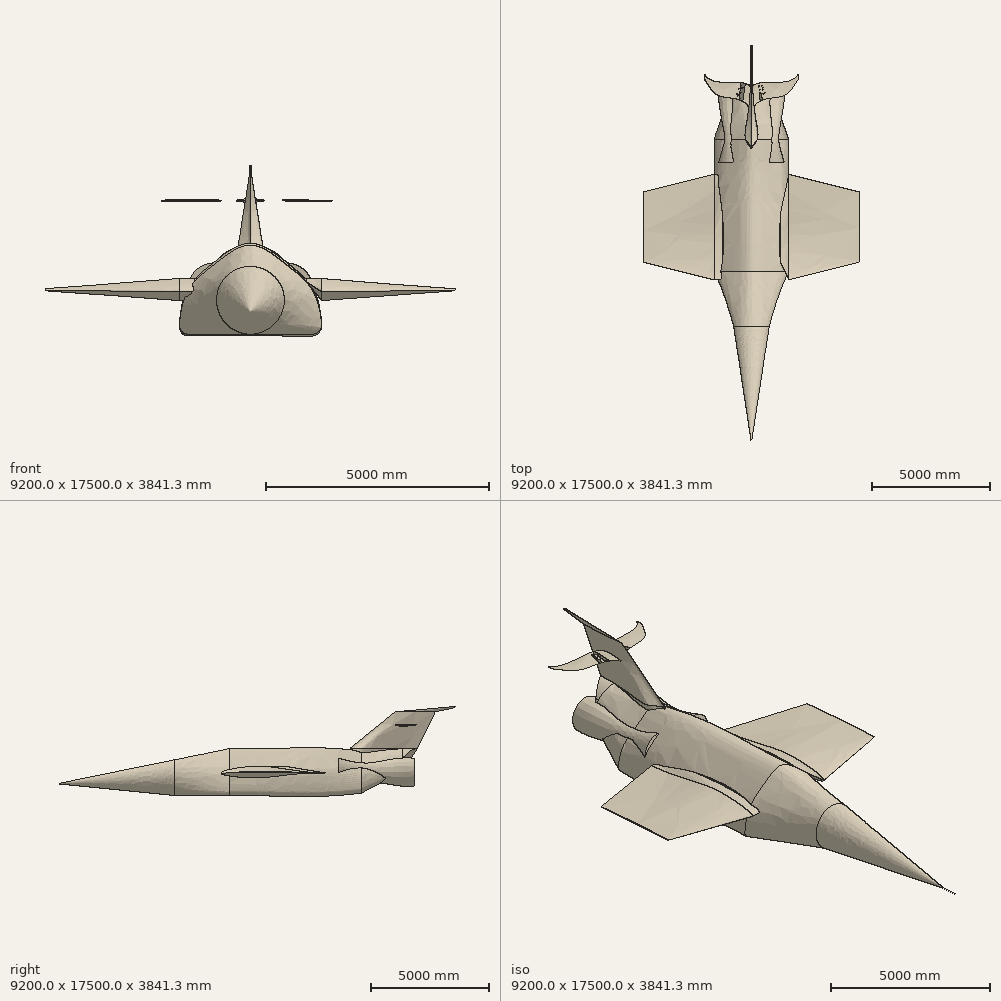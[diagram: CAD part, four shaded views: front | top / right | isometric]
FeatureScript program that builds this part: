
annotation { "Feature Type Name" : "Feature", "Feature Type Description" : "" }
export const myFeature = defineFeature(function(context is Context, id is Id, definition is map)
    precondition{}
    {
        {
            var Q0;
            Q0=qCreatedBy(makeId("Right.planeOp"),FACE);
            var sketch = newSketch(context, id + "F0", { "sketchPlane" : qUnion([Q0])});
            skLineSegment(sketch, "E0", {"start": v(0, 0) * mm, "end": v(-1750, 0) * mm});
            skLineSegment(sketch, "E1", {"start": v(-1750, 0) * mm, "end": v(-3500, 0) * mm});
            skLineSegment(sketch, "E2", {"start": v(-3500, 0) * mm, "end": v(-3500, -1000) * mm});
            skLineSegment(sketch, "E3", {"start": v(-3500, -1000) * mm, "end": v(-8500, -1000) * mm});
            skLineSegment(sketch, "E4", {"start": v(-8500, -1000) * mm, "end": v(-8500, -499.31) * mm});
            skLineSegment(sketch, "E5", {"start": v(-1151.4, 0) * mm, "end": v(-1151.4, 1000) * mm});
            skLineSegment(sketch, "E6", {"start": v(-1151.4, 1000) * mm, "end": v(-8500, -499.31) * mm});
            skLineSegment(sketch, "E7", {"start": v(-8500, -499.31) * mm, "end": v(-3500, -1000) * mm});
            skLineSegment(sketch, "E8", {"start": v(-3500, 0) * mm, "end": v(-3500, 520.82) * mm});
            skLineSegment(sketch, "E9", {"start": v(-8500, -499.31) * mm, "end": v(-8450, -499.31) * mm});
            skLineSegment(sketch, "E10", {"start": v(-8450, -499.31) * mm, "end": v(-8450, -489.1) * mm});
            skLineSegment(sketch, "E11", {"start": v(-8450, -499.31) * mm, "end": v(-8450, -504.32) * mm});
            skSolve(sketch);
        }
        {
            var Q0;
            Q0=sQuery(id+"F0.wireOp",EDGE,"E5");
            cPlane(context, id + "F1", {"entities" : qUnion([Q0]), "cplaneType" : CPlaneType.LINE_ANGLE, "offset" : 25 * mm, "angle" : 90 * degree, "oppositeDirection" : true, "width" : 150 * mm, "height" : 150 * mm});
        }
        {
            var Q0;
            Q0=qCreatedBy(id+"F1.planeOp",FACE);
            var sketch = newSketch(context, id + "F2", { "sketchPlane" : qUnion([Q0])});
            skLineSegment(sketch, "E12.top", {"start": v(-1394.2, -1000) * mm, "end": v(1394.2, -1000) * mm});
            skPoint(sketch, "E12.middle", {"position": v(0, 0) * mm});
            skFitSpline(sketch, "E13", {"points": [v(-1600, -1000) * mm, v(-848, 530) * mm, v(0, 1000) * mm, v(848, 530) * mm, v(1600, -1000) * mm], "startDerivative": vector(0, 10524.75) * mm, "endDerivative": vector(0, -10524.75) * mm});
            skArc(sketch, "E14", {"start": v(-735.27, 618.52) * mm, "mid": v(-1273.27, 435.52) * mm, "end": v(-1440.68, -107.53) * mm});
            skArc(sketch, "E15", {"start": v(1440.68, -107.53) * mm, "mid": v(1273.27, 435.52) * mm, "end": v(735.27, 618.52) * mm});
            skFitSpline(sketch, "E16.trimOffspring", {"points": [v(-1600, -1000) * mm, v(-848, 530) * mm, v(0, 1000) * mm, v(848, 530) * mm, v(1600, -1000) * mm], "startDerivative": vector(0, 10524.75) * mm, "endDerivative": vector(0, -10524.75) * mm});
            skFitSpline(sketch, "E17.trimOffspring", {"points": [v(-1600, -1000) * mm, v(-848, 530) * mm, v(0, 1000) * mm, v(848, 530) * mm, v(1600, -1000) * mm], "startDerivative": vector(0, 10524.75) * mm, "endDerivative": vector(0, -10524.75) * mm});
            skArc(sketch, "E18.filletArc", {"start": v(-1593.82, -787.83) * mm, "mid": v(-1539.85, -937.05) * mm, "end": v(-1394.2, -1000) * mm});
            skArc(sketch, "E19.filletArc", {"start": v(1394.2, -1000) * mm, "mid": v(1539.85, -937.05) * mm, "end": v(1593.82, -787.83) * mm});
            skSolve(sketch);
        }
        {
            var Q0;
            Q0=qCreatedBy(makeId("Front.planeOp"),FACE);
            var sketch = newSketch(context, id + "F3", { "sketchPlane" : qUnion([Q0])});
            skLineSegment(sketch, "E20.top", {"start": v(-1394.2, -1000) * mm, "end": v(1394.2, -1000) * mm});
            skPoint(sketch, "E20.middle", {"position": v(0, 0) * mm});
            skFitSpline(sketch, "E21", {"points": [v(-1600, -1000) * mm, v(-848, 530) * mm, v(0, 1000) * mm, v(848, 530) * mm, v(1600, -1000) * mm], "startDerivative": vector(0, 10524.75) * mm, "endDerivative": vector(0, -10524.75) * mm});
            skArc(sketch, "E22", {"start": v(-735.27, 618.52) * mm, "mid": v(-1273.27, 435.52) * mm, "end": v(-1440.68, -107.53) * mm});
            skArc(sketch, "E23", {"start": v(1440.68, -107.53) * mm, "mid": v(1273.27, 435.52) * mm, "end": v(735.27, 618.52) * mm});
            skFitSpline(sketch, "E24.trimOffspring", {"points": [v(-1600, -1000) * mm, v(-848, 530) * mm, v(0, 1000) * mm, v(848, 530) * mm, v(1600, -1000) * mm], "startDerivative": vector(0, 10524.75) * mm, "endDerivative": vector(0, -10524.75) * mm});
            skFitSpline(sketch, "E25.trimOffspring", {"points": [v(-1600, -1000) * mm, v(-848, 530) * mm, v(0, 1000) * mm, v(848, 530) * mm, v(1600, -1000) * mm], "startDerivative": vector(0, 10524.75) * mm, "endDerivative": vector(0, -10524.75) * mm});
            skArc(sketch, "E26.filletArc", {"start": v(-1593.82, -787.83) * mm, "mid": v(-1539.85, -937.05) * mm, "end": v(-1394.2, -1000) * mm});
            skArc(sketch, "E27.filletArc", {"start": v(1394.2, -1000) * mm, "mid": v(1539.85, -937.05) * mm, "end": v(1593.82, -787.83) * mm});
            skSolve(sketch);
        }
        {
            var Q0;
            Q0=qCreatedBy(makeId("Front.planeOp"),FACE);
            cPlane(context, id + "F4", {"entities" : qUnion([Q0]), "cplaneType" : CPlaneType.OFFSET, "offset" : 3500 * mm, "oppositeDirection" : true, "width" : 150 * mm, "height" : 150 * mm});
        }
        {
            var Q0;
            Q0=qCreatedBy(id+"F4.planeOp",FACE);
            var sketch = newSketch(context, id + "F5", { "sketchPlane" : qUnion([Q0])});
            skLineSegment(sketch, "E28.top", {"start": v(-1394.2, -1000) * mm, "end": v(1394.2, -1000) * mm});
            skPoint(sketch, "E28.middle", {"position": v(0, 0) * mm});
            skFitSpline(sketch, "E29", {"points": [v(-1600, -1000) * mm, v(-848, 530) * mm, v(0, 1000) * mm, v(848, 530) * mm, v(1600, -1000) * mm], "startDerivative": vector(0, 10524.75) * mm, "endDerivative": vector(0, -10524.75) * mm});
            skArc(sketch, "E30", {"start": v(-735.27, 618.52) * mm, "mid": v(-1273.27, 435.52) * mm, "end": v(-1440.68, -107.53) * mm});
            skArc(sketch, "E31", {"start": v(1440.68, -107.53) * mm, "mid": v(1273.27, 435.52) * mm, "end": v(735.27, 618.52) * mm});
            skFitSpline(sketch, "E32.trimOffspring", {"points": [v(-1600, -1000) * mm, v(-848, 530) * mm, v(0, 1000) * mm, v(848, 530) * mm, v(1600, -1000) * mm], "startDerivative": vector(0, 10524.75) * mm, "endDerivative": vector(0, -10524.75) * mm});
            skFitSpline(sketch, "E33.trimOffspring", {"points": [v(-1600, -1000) * mm, v(-848, 530) * mm, v(0, 1000) * mm, v(848, 530) * mm, v(1600, -1000) * mm], "startDerivative": vector(0, 10524.75) * mm, "endDerivative": vector(0, -10524.75) * mm});
            skArc(sketch, "E34.filletArc", {"start": v(-1593.82, -787.83) * mm, "mid": v(-1539.85, -937.05) * mm, "end": v(-1394.2, -1000) * mm});
            skArc(sketch, "E35.filletArc", {"start": v(1394.2, -1000) * mm, "mid": v(1539.85, -937.05) * mm, "end": v(1593.82, -787.83) * mm});
            skSolve(sketch);
        }
        {
            var Q0;
            Q0=qCreatedBy(makeId("Front.planeOp"),FACE);
            cPlane(context, id + "F6", {"entities" : qUnion([Q0]), "cplaneType" : CPlaneType.OFFSET, "offset" : 4500 * mm, "oppositeDirection" : true, "width" : 150 * mm, "height" : 150 * mm});
        }
        {
            var Q0;
            Q0=qCreatedBy(id+"F6.planeOp",FACE);
            var sketch = newSketch(context, id + "F7", { "sketchPlane" : qUnion([Q0])});
            skLineSegment(sketch, "E36.top", {"start": v(-1413.07, -900) * mm, "end": v(1413.07, -900) * mm});
            skPoint(sketch, "E36.middle", {"position": v(0, 0) * mm});
            skFitSpline(sketch, "E37", {"points": [v(-1600, -900) * mm, v(-784.42, 441.24) * mm, v(0, 900) * mm, v(784.42, 441.24) * mm, v(1600, -900) * mm], "startDerivative": vector(0, 9508.62) * mm, "endDerivative": vector(0, -9508.62) * mm});
            skArc(sketch, "E38", {"start": v(-719.25, 488.69) * mm, "mid": v(-1131.76, 394.84) * mm, "end": v(-1324.66, 18.33) * mm});
            skArc(sketch, "E39", {"start": v(1324.66, 18.33) * mm, "mid": v(1131.76, 394.84) * mm, "end": v(719.25, 488.69) * mm});
            skFitSpline(sketch, "E40.trimOffspring", {"points": [v(-1600, -900) * mm, v(-784.42, 441.24) * mm, v(0, 900) * mm, v(784.42, 441.24) * mm, v(1600, -900) * mm], "startDerivative": vector(0, 9508.62) * mm, "endDerivative": vector(0, -9508.62) * mm});
            skFitSpline(sketch, "E41.trimOffspring", {"points": [v(-1600, -900) * mm, v(-784.42, 441.24) * mm, v(0, 900) * mm, v(784.42, 441.24) * mm, v(1600, -900) * mm], "startDerivative": vector(0, 9508.62) * mm, "endDerivative": vector(0, -9508.62) * mm});
            skArc(sketch, "E42.filletArc", {"start": v(-1592.48, -705.43) * mm, "mid": v(-1545.4, -842.02) * mm, "end": v(-1413.07, -900) * mm});
            skArc(sketch, "E43.filletArc", {"start": v(1413.07, -900) * mm, "mid": v(1545.4, -842.02) * mm, "end": v(1592.48, -705.43) * mm});
            skLineSegment(sketch, "E44", {"start": v(-719.25, 488.69) * mm, "end": v(-1324.66, 18.33) * mm, "construction": true});
            skLineSegment(sketch, "E45", {"start": v(719.25, 488.69) * mm, "end": v(1324.66, 18.33) * mm, "construction": true});
            skSolve(sketch);
        }
        {
            var Q0;
            Q0=qCreatedBy(makeId("Front.planeOp"),FACE);
            cPlane(context, id + "F8", {"entities" : qUnion([Q0]), "cplaneType" : CPlaneType.OFFSET, "offset" : 6232.05 * mm, "oppositeDirection" : true, "width" : 150 * mm, "height" : 150 * mm});
        }
        {
            var Q0;
            Q0=qCreatedBy(id+"F8.planeOp",FACE);
            var sketch = newSketch(context, id + "F9", { "sketchPlane" : qUnion([Q0])});
            skArc(sketch, "E46", {"start": v(998.61, 52.63) * mm, "mid": v(0, 1000) * mm, "end": v(-998.61, 52.63) * mm});
            skLineSegment(sketch, "E47", {"start": v(0, 0) * mm, "end": v(-948.68, 0) * mm});
            skLineSegment(sketch, "E48", {"start": v(0, 0) * mm, "end": v(948.68, 0) * mm});
            skLineSegment(sketch, "E49", {"start": v(0, 1000) * mm, "end": v(0, 675) * mm, "construction": true});
            skLineSegment(sketch, "E50", {"start": v(0, 675) * mm, "end": v(-737.82, 675) * mm, "construction": true});
            skLineSegment(sketch, "E51", {"start": v(0, 675) * mm, "end": v(737.82, 675) * mm, "construction": true});
            skPoint(sketch, "E52.visualSharp", {"position": v(-1000, 0) * mm});
            skArc(sketch, "E52.filletArc", {"start": v(-998.61, 52.63) * mm, "mid": v(-984.96, 15.59) * mm, "end": v(-948.68, 0) * mm});
            skPoint(sketch, "E53.visualSharp", {"position": v(1000, 0) * mm});
            skArc(sketch, "E53.filletArc", {"start": v(948.68, 0) * mm, "mid": v(984.96, 15.59) * mm, "end": v(998.61, 52.63) * mm});
            skSolve(sketch);
        }
        {
            var Q0;
            Q0=makeQuery(id+"F2.imprint","IMPRINT",FACE,{"disambiguationData":[TD([[makeQuery(id+"F2.imprint","IMPRINT",EDGE,{"derivedFrom":sQuery(id+"F2.wireOp",EDGE,"E12.top")}),1.0]])]});
            var Q1;
            Q1=makeQuery(id+"F3.imprint","IMPRINT",FACE,{"disambiguationData":[TD([[makeQuery(id+"F3.imprint","IMPRINT",EDGE,{"derivedFrom":sQuery(id+"F3.wireOp",EDGE,"E20.top")}),1.0]])]});
            var Q2;
            Q2=makeQuery(id+"F5.imprint","IMPRINT",FACE,{"disambiguationData":[TD([[makeQuery(id+"F5.imprint","IMPRINT",EDGE,{"derivedFrom":sQuery(id+"F5.wireOp",EDGE,"E28.top")}),1.0]])]});
            var Q3;
            Q3=makeQuery(id+"F7.imprint","IMPRINT",FACE,{"disambiguationData":[TD([[makeQuery(id+"F7.imprint","IMPRINT",EDGE,{"derivedFrom":sQuery(id+"F7.wireOp",EDGE,"E36.top")}),1.0]])]});
            loft(context, id + "F10", {"sheetProfilesArray" : [{ "sheetProfileEntities" : qUnion([Q0]) }, { "sheetProfileEntities" : qUnion([Q1]) }, { "sheetProfileEntities" : qUnion([Q2]) }, { "sheetProfileEntities" : qUnion([Q3]) }]});
        }
        {
            var Q0;
            Q0=sQuery(id+"F7.wireOp",EDGE,"E44");
            var Q1;
            Q1=sQuery(id+"F9.wireOp",VERTEX,"E50.end");
            cPlane(context, id + "F11", {"entities" : qUnion([Q0, Q1]), "cplaneType" : CPlaneType.LINE_ANGLE, "offset" : 25 * mm, "angle" : 180 * degree, "width" : 150 * mm, "height" : 150 * mm});
        }
        {
            var Q0;
            Q0=qCreatedBy(id+"F11.planeOp",FACE);
            var sketch = newSketch(context, id + "F12", { "sketchPlane" : qUnion([Q0])});
            skLineSegment(sketch, "E54", {"start": v(-589.34, 4526.34) * mm, "end": v(-612.8, 6268.32) * mm});
            skLineSegment(sketch, "E55", {"start": v(-1354.08, 4472.19) * mm, "end": v(-612.8, 6268.32) * mm});
            skSolve(sketch);
        }
        {
            var Q0;
            Q0=sQuery(id+"F7.wireOp",EDGE,"E45");
            var Q1;
            Q1=sQuery(id+"F9.wireOp",VERTEX,"E51.end");
            cPlane(context, id + "F13", {"entities" : qUnion([Q0, Q1]), "cplaneType" : CPlaneType.LINE_ANGLE, "offset" : 25 * mm, "angle" : 0 * degree, "width" : 150 * mm, "height" : 150 * mm});
        }
        {
            var Q0;
            Q0=qCreatedBy(id+"F13.planeOp",FACE);
            var sketch = newSketch(context, id + "F14", { "sketchPlane" : qUnion([Q0])});
            skLineSegment(sketch, "E56", {"start": v(589.34, 4526.34) * mm, "end": v(612.8, 6268.32) * mm});
            skLineSegment(sketch, "E57", {"start": v(1354.08, 4472.19) * mm, "end": v(612.8, 6268.32) * mm});
            skSolve(sketch);
        }
        {
            var Q1;
            Q1=makeQuery(id+"F10.opLoft","CAP_FACE",FACE,{"disambiguationData":[OSD([makeQuery(id+"F7.imprint","IMPRINT",FACE,{"disambiguationData":[TD([[makeQuery(id+"F7.imprint","IMPRINT",EDGE,{"derivedFrom":sQuery(id+"F7.wireOp",EDGE,"E36.top")}),1.0]])]})])],"isStart":true});
            var Q2;
            Q2=makeQuery(id+"F9.imprint","IMPRINT",FACE,{"disambiguationData":[TD([[makeQuery(id+"F9.imprint","IMPRINT",EDGE,{"derivedFrom":sQuery(id+"F9.wireOp",EDGE,"E46")}),1.0]])]});
            var Q3;
            Q3=sQuery(id+"F12.wireOp",EDGE,"E54");
            var Q4;
            Q4=sQuery(id+"F14.wireOp",EDGE,"E56");
            loft(context, id + "F15", {"operationType" : NewBodyOperationType.ADD, "addGuides" : true, "sheetProfilesArray" : [{ "sheetProfileEntities" : qUnion([Q1]) }, { "sheetProfileEntities" : qUnion([Q2]) }], "guidesArray" : [{ "guideEntities" : qUnion([Q3]), "guideDerivativeType" : LoftGuideDerivativeType.DEFAULT, "guideDerivativeMagnitude" : 1 }, { "guideEntities" : qUnion([Q4]), "guideDerivativeType" : LoftGuideDerivativeType.DEFAULT, "guideDerivativeMagnitude" : 1 }]});
        }
        {
            var Q0;
            Q0=makeQuery(id+"F15.opLoft","CAP_FACE",FACE,{"disambiguationData":[OSD([makeQuery(id+"F9.imprint","IMPRINT",FACE,{"disambiguationData":[TD([[makeQuery(id+"F9.imprint","IMPRINT",EDGE,{"derivedFrom":sQuery(id+"F9.wireOp",EDGE,"E46")}),1.0]])]})])],"isStart":true});
            extrude(context, id + "F16", {"entities" : qUnion([Q0]), "operationType" : NewBodyOperationType.ADD, "depth" : 649.4 * mm, "offsetDistance" : 25 * mm});
        }
        {
            var Q0;
            Q0=qCreatedBy(makeId("Right.planeOp"),FACE);
            var sketch = newSketch(context, id + "F17", { "sketchPlane" : qUnion([Q0])});
            skLineSegment(sketch, "E58", {"start": v(0, 0) * mm, "end": v(4500, 0) * mm});
            skLineSegment(sketch, "E59", {"start": v(4500, 0) * mm, "end": v(6232.05, 0) * mm});
            skLineSegment(sketch, "E60", {"start": v(4500, 0) * mm, "end": v(4500, 1000) * mm});
            skLineSegment(sketch, "E61", {"start": v(4500, 1000) * mm, "end": v(6881.46, 1000) * mm});
            skLineSegment(sketch, "E62", {"start": v(6881.46, 1000) * mm, "end": v(6881.46, -1000) * mm});
            skLineSegment(sketch, "E63", {"start": v(6881.46, 1000) * mm, "end": v(6232.05, 0) * mm});
            skLineSegment(sketch, "E64", {"start": v(6232.05, 0) * mm, "end": v(5582.64, -1000) * mm});
            skLineSegment(sketch, "E65", {"start": v(5582.64, -1000) * mm, "end": v(6881.46, -1000) * mm});
            skSolve(sketch);
        }
        {
            var Q0;
            Q0=makeQuery(id+"F17.imprint","IMPRINT",FACE,{"disambiguationData":[TD([[makeQuery(id+"F17.imprint","IMPRINT",EDGE,{"derivedFrom":sQuery(id+"F17.wireOp",EDGE,"E62")}),-1.0]])]});
            var Q1;
            Q1=sQuery(id+"F17.wireOp",EDGE,"E61");
            revolve(context, id + "F18", {"operationType" : NewBodyOperationType.REMOVE, "entities" : qUnion([Q0]), "axis" : qUnion([Q1]), "revolveType" : RevolveType.SYMMETRIC, "oppositeDirection" : true, "angle" : 182 * degree});
        }
        {
            var Q0;
            Q0=qCreatedBy(id+"F1.planeOp",FACE);
            var sketch = newSketch(context, id + "F19", { "sketchPlane" : qUnion([Q0])});
            skLineSegment(sketch, "E66.top", {"start": v(-1394.2, -1000) * mm, "end": v(1394.2, -1000) * mm});
            skPoint(sketch, "E66.middle", {"position": v(0, 0) * mm});
            skFitSpline(sketch, "E67", {"points": [v(-1600, -1000) * mm, v(-848, 530) * mm, v(0, 1000) * mm, v(848, 530) * mm, v(1600, -1000) * mm], "startDerivative": vector(0, 10524.75) * mm, "endDerivative": vector(0, -10524.75) * mm});
            skArc(sketch, "E68.filletArc", {"start": v(-1593.82, -787.83) * mm, "mid": v(-1539.85, -937.05) * mm, "end": v(-1394.2, -1000) * mm});
            skArc(sketch, "E69.filletArc", {"start": v(1394.2, -1000) * mm, "mid": v(1539.85, -937.05) * mm, "end": v(1593.82, -787.83) * mm});
            skLineSegment(sketch, "E70", {"start": v(-1593.82, -787.83) * mm, "end": v(-1394.2, -1000) * mm, "construction": true});
            skLineSegment(sketch, "E71", {"start": v(1593.82, -787.83) * mm, "end": v(1394.2, -1000) * mm, "construction": true});
            skSolve(sketch);
        }
        {
            var Q0;
            Q0=qCreatedBy(makeId("Front.planeOp"),FACE);
            cPlane(context, id + "F20", {"entities" : qUnion([Q0]), "cplaneType" : CPlaneType.OFFSET, "offset" : 3500 * mm, "width" : 150 * mm, "height" : 150 * mm});
        }
        {
            var Q0;
            Q0=qCreatedBy(id+"F20.planeOp",FACE);
            var sketch = newSketch(context, id + "F21", { "sketchPlane" : qUnion([Q0])});
            skCircle(sketch, "E72", {"center": v(0, -239.59) * mm, "radius": 760.41 * mm});
            skLineSegment(sketch, "E73", {"start": v(0, -1000) * mm, "end": v(0, -800) * mm, "construction": true});
            skLineSegment(sketch, "E74", {"start": v(0, -800) * mm, "end": v(-513.97, -800) * mm, "construction": true});
            skLineSegment(sketch, "E75", {"start": v(0, -800) * mm, "end": v(513.97, -800) * mm, "construction": true});
            skSolve(sketch);
        }
        {
            var Q0;
            Q0=qCreatedBy(makeId("Front.planeOp"),FACE);
            cPlane(context, id + "F22", {"entities" : qUnion([Q0]), "cplaneType" : CPlaneType.OFFSET, "offset" : 8450 * mm, "width" : 150 * mm, "height" : 150 * mm});
        }
        {
            var Q0;
            Q0=qCreatedBy(id+"F22.planeOp",FACE);
            var sketch = newSketch(context, id + "F23", { "sketchPlane" : qUnion([Q0])});
            skCircle(sketch, "E76", {"center": v(0, -496.71) * mm, "radius": 7.6 * mm});
            skSolve(sketch);
        }
        {
            var Q0;
            Q0=sQuery(id+"F19.wireOp",EDGE,"E70");
            var Q1;
            Q1=sQuery(id+"F21.wireOp",VERTEX,"E74.end");
            cPlane(context, id + "F24", {"entities" : qUnion([Q0, Q1]), "cplaneType" : CPlaneType.LINE_ANGLE, "offset" : 25 * mm, "angle" : 0 * degree, "width" : 150 * mm, "height" : 150 * mm});
        }
        {
            var Q0;
            Q0=qCreatedBy(id+"F24.planeOp",FACE);
            var sketch = newSketch(context, id + "F25", { "sketchPlane" : qUnion([Q0])});
            skLineSegment(sketch, "E77", {"start": v(3032.27, -230.44) * mm, "end": v(558.11, 518.4) * mm});
            skLineSegment(sketch, "E78", {"start": v(3032.27, -230.44) * mm, "end": v(558.11, 227.09) * mm});
            skSolve(sketch);
        }
        {
            var Q0;
            Q0=sQuery(id+"F19.wireOp",EDGE,"E71");
            var Q1;
            Q1=sQuery(id+"F21.wireOp",VERTEX,"E75.end");
            cPlane(context, id + "F26", {"entities" : qUnion([Q0, Q1]), "cplaneType" : CPlaneType.LINE_ANGLE, "offset" : 25 * mm, "angle" : 180 * degree, "width" : 150 * mm, "height" : 150 * mm});
        }
        {
            var Q0;
            Q0=qCreatedBy(id+"F26.planeOp",FACE);
            var sketch = newSketch(context, id + "F27", { "sketchPlane" : qUnion([Q0])});
            skLineSegment(sketch, "E79", {"start": v(-3032.27, -230.44) * mm, "end": v(-558.11, 518.4) * mm});
            skLineSegment(sketch, "E80", {"start": v(-3032.27, -230.44) * mm, "end": v(-558.11, 227.09) * mm});
            skSolve(sketch);
        }
        {
            var Q1;
            Q1=makeQuery(id+"F19.imprint","IMPRINT",FACE,{"disambiguationData":[TD([[makeQuery(id+"F19.imprint","IMPRINT",EDGE,{"derivedFrom":sQuery(id+"F19.wireOp",EDGE,"E66.top")}),1.0]])]});
            var Q2;
            Q2=makeQuery(id+"F21.imprint","IMPRINT",FACE,{"disambiguationData":[TD([[makeQuery(id+"F21.imprint","IMPRINT",EDGE,{"derivedFrom":sQuery(id+"F21.wireOp",EDGE,"E72")}),1.0]])]});
            var Q3;
            Q3=sQuery(id+"F25.wireOp",EDGE,"E77");
            var Q4;
            Q4=sQuery(id+"F27.wireOp",EDGE,"E79");
            loft(context, id + "F28", {"operationType" : NewBodyOperationType.ADD, "addGuides" : true, "sheetProfilesArray" : [{ "sheetProfileEntities" : qUnion([Q1]) }, { "sheetProfileEntities" : qUnion([Q2]) }], "guidesArray" : [{ "guideEntities" : qUnion([Q3]), "guideDerivativeType" : LoftGuideDerivativeType.DEFAULT, "guideDerivativeMagnitude" : 1 }, { "guideEntities" : qUnion([Q4]), "guideDerivativeType" : LoftGuideDerivativeType.DEFAULT, "guideDerivativeMagnitude" : 1 }]});
        }
        {
            var Q1;
            Q1=makeQuery(id+"F28.opLoft","CAP_FACE",FACE,{"disambiguationData":[OSD([makeQuery(id+"F21.imprint","IMPRINT",FACE,{"disambiguationData":[TD([[makeQuery(id+"F21.imprint","IMPRINT",EDGE,{"derivedFrom":sQuery(id+"F21.wireOp",EDGE,"E72")}),1.0]])]})])],"isStart":true});
            var Q2;
            Q2=makeQuery(id+"F23.imprint","IMPRINT",FACE,{"disambiguationData":[TD([[makeQuery(id+"F23.imprint","IMPRINT",EDGE,{"derivedFrom":sQuery(id+"F23.wireOp",EDGE,"E76")}),1.0]])]});
            loft(context, id + "F29", {"operationType" : NewBodyOperationType.ADD, "sheetProfilesArray" : [{ "sheetProfileEntities" : qUnion([Q1]) }, { "sheetProfileEntities" : qUnion([Q2]) }]});
        }
        {
            var Q0;
            Q0=makeQuery(id+"F29.opLoft","CAP_FACE",FACE,{"disambiguationData":[OSD([makeQuery(id+"F23.imprint","IMPRINT",FACE,{"disambiguationData":[TD([[makeQuery(id+"F23.imprint","IMPRINT",EDGE,{"derivedFrom":sQuery(id+"F23.wireOp",EDGE,"E76")}),1.0]])]})])],"isStart":true});
            extrude(context, id + "F30", {"entities" : qUnion([Q0]), "operationType" : NewBodyOperationType.ADD, "depth" : 550 * mm, "offsetDistance" : 25 * mm});
        }
        {
            var Q0;
            Q0=qCreatedBy(makeId("Front.planeOp"),FACE);
            cPlane(context, id + "F31", {"entities" : qUnion([Q0]), "cplaneType" : CPlaneType.OFFSET, "offset" : 3500 * mm, "oppositeDirection" : true, "width" : 150 * mm, "height" : 150 * mm});
        }
        {
            var Q0;
            Q0=qCreatedBy(id+"F31.planeOp",FACE);
            var sketch = newSketch(context, id + "F32", { "sketchPlane" : qUnion([Q0])});
            skCircle(sketch, "E81", {"center": v(-800, 0) * mm, "radius": 600 * mm});
            skCircle(sketch, "E82", {"center": v(800, 0) * mm, "radius": 600 * mm});
            skSolve(sketch);
        }
        {
            var Q0;
            Q0=qCreatedBy(makeId("Front.planeOp"),FACE);
            cPlane(context, id + "F33", {"entities" : qUnion([Q0]), "cplaneType" : CPlaneType.OFFSET, "offset" : 4500 * mm, "oppositeDirection" : true, "width" : 150 * mm, "height" : 150 * mm});
        }
        {
            var Q0;
            Q0=qCreatedBy(id+"F33.planeOp",FACE);
            var sketch = newSketch(context, id + "F34", { "sketchPlane" : qUnion([Q0])});
            skCircle(sketch, "E83", {"center": v(-800, 0) * mm, "radius": 400 * mm});
            skCircle(sketch, "E84", {"center": v(800, 0) * mm, "radius": 400 * mm});
            skSolve(sketch);
        }
        {
            var Q0;
            Q0=qCreatedBy(makeId("Front.planeOp"),FACE);
            cPlane(context, id + "F35", {"entities" : qUnion([Q0]), "cplaneType" : CPlaneType.OFFSET, "offset" : 6232.05 * mm, "oppositeDirection" : true, "width" : 150 * mm, "height" : 150 * mm});
        }
        {
            var Q0;
            Q0=qCreatedBy(id+"F35.planeOp",FACE);
            var sketch = newSketch(context, id + "F36", { "sketchPlane" : qUnion([Q0])});
            skCircle(sketch, "E85", {"center": v(-800, 0) * mm, "radius": 600 * mm});
            skCircle(sketch, "E86", {"center": v(800, 0) * mm, "radius": 600 * mm});
            skSolve(sketch);
        }
        {
            var Q0;
            Q0=qCreatedBy(makeId("Front.planeOp"),FACE);
            cPlane(context, id + "F37", {"entities" : qUnion([Q0]), "cplaneType" : CPlaneType.OFFSET, "offset" : 6732.05 * mm, "oppositeDirection" : true, "width" : 150 * mm, "height" : 150 * mm});
        }
        {
            var Q0;
            Q0=qCreatedBy(id+"F37.planeOp",FACE);
            var sketch = newSketch(context, id + "F38", { "sketchPlane" : qUnion([Q0])});
            skCircle(sketch, "E87", {"center": v(-800, 0) * mm, "radius": 600 * mm});
            skCircle(sketch, "E88", {"center": v(800, 0) * mm, "radius": 600 * mm});
            skSolve(sketch);
        }
        {
            var Q0;
            Q0=makeQuery(id+"F32.imprint","IMPRINT",FACE,{"disambiguationData":[TD([[makeQuery(id+"F32.imprint","IMPRINT",EDGE,{"derivedFrom":sQuery(id+"F32.wireOp",EDGE,"E81")}),1.0]])]});
            var Q1;
            Q1=makeQuery(id+"F34.imprint","IMPRINT",FACE,{"disambiguationData":[TD([[makeQuery(id+"F34.imprint","IMPRINT",EDGE,{"derivedFrom":sQuery(id+"F34.wireOp",EDGE,"E83")}),1.0]])]});
            var Q2;
            Q2=makeQuery(id+"F36.imprint","IMPRINT",FACE,{"disambiguationData":[TD([[makeQuery(id+"F36.imprint","IMPRINT",EDGE,{"derivedFrom":sQuery(id+"F36.wireOp",EDGE,"E85")}),1.0]])]});
            var Q3;
            Q3=makeQuery(id+"F38.imprint","IMPRINT",FACE,{"disambiguationData":[TD([[makeQuery(id+"F38.imprint","IMPRINT",EDGE,{"derivedFrom":sQuery(id+"F38.wireOp",EDGE,"E87")}),1.0]])]});
            loft(context, id + "F39", {"sheetProfilesArray" : [{ "sheetProfileEntities" : qUnion([Q0]) }, { "sheetProfileEntities" : qUnion([Q1]) }, { "sheetProfileEntities" : qUnion([Q2]) }, { "sheetProfileEntities" : qUnion([Q3]) }]});
        }
        {
            var Q0;
            Q0=makeQuery(id+"F32.imprint","IMPRINT",FACE,{"disambiguationData":[TD([[makeQuery(id+"F32.imprint","IMPRINT",EDGE,{"derivedFrom":sQuery(id+"F32.wireOp",EDGE,"E82")}),1.0]])]});
            var Q1;
            Q1=makeQuery(id+"F34.imprint","IMPRINT",FACE,{"disambiguationData":[TD([[makeQuery(id+"F34.imprint","IMPRINT",EDGE,{"derivedFrom":sQuery(id+"F34.wireOp",EDGE,"E84")}),1.0]])]});
            var Q2;
            Q2=makeQuery(id+"F36.imprint","IMPRINT",FACE,{"disambiguationData":[TD([[makeQuery(id+"F36.imprint","IMPRINT",EDGE,{"derivedFrom":sQuery(id+"F36.wireOp",EDGE,"E86")}),1.0]])]});
            var Q3;
            Q3=makeQuery(id+"F38.imprint","IMPRINT",FACE,{"disambiguationData":[TD([[makeQuery(id+"F38.imprint","IMPRINT",EDGE,{"derivedFrom":sQuery(id+"F38.wireOp",EDGE,"E88")}),1.0]])]});
            loft(context, id + "F40", {"sheetProfilesArray" : [{ "sheetProfileEntities" : qUnion([Q0]) }, { "sheetProfileEntities" : qUnion([Q1]) }, { "sheetProfileEntities" : qUnion([Q2]) }, { "sheetProfileEntities" : qUnion([Q3]) }]});
        }
        {
            var Q0;
            Q0=qCreatedBy(makeId("Right.planeOp"),FACE);
            var sketch = newSketch(context, id + "F41", { "sketchPlane" : qUnion([Q0])});
            skFitSpline(sketch, "E89", {"points": [v(-1500, -50) * mm, v(0, 250) * mm, v(3000, -50) * mm, v(0, -250) * mm, v(-1500, -50) * mm]});
            skSolve(sketch);
        }
        {
            var Q0;
            Q0=qCreatedBy(makeId("Right.planeOp"),FACE);
            cPlane(context, id + "F42", {"entities" : qUnion([Q0]), "cplaneType" : CPlaneType.OFFSET, "offset" : 1600 * mm, "oppositeDirection" : true, "width" : 150 * mm, "height" : 150 * mm});
        }
        {
            var Q0;
            Q0=qCreatedBy(id+"F42.planeOp",FACE);
            var sketch = newSketch(context, id + "F43", { "sketchPlane" : qUnion([Q0])});
            skFitSpline(sketch, "E90", {"points": [v(-1500, -50) * mm, v(0, 250) * mm, v(3000, -50) * mm], "startDerivative": vector(0, 887.04) * mm, "endDerivative": vector(7705.35, -256.85) * mm});
            skFitSpline(sketch, "E91", {"points": [v(-1500, -50) * mm, v(0, -250) * mm, v(3000, -50) * mm], "startDerivative": vector(0, -722.87) * mm, "endDerivative": vector(7692.49, -256.42) * mm});
            skSolve(sketch);
        }
        {
            var Q0;
            Q0=qCreatedBy(makeId("Right.planeOp"),FACE);
            cPlane(context, id + "F44", {"entities" : qUnion([Q0]), "cplaneType" : CPlaneType.OFFSET, "offset" : 1600 * mm, "width" : 150 * mm, "height" : 150 * mm});
        }
        {
            var Q0;
            Q0=qCreatedBy(id+"F44.planeOp",FACE);
            var sketch = newSketch(context, id + "F45", { "sketchPlane" : qUnion([Q0])});
            skFitSpline(sketch, "E92", {"points": [v(-1500, -50) * mm, v(0, 250) * mm, v(3000, -50) * mm], "startDerivative": vector(0, 887.04) * mm, "endDerivative": vector(7705.35, -256.85) * mm});
            skFitSpline(sketch, "E93", {"points": [v(-1500, -50) * mm, v(0, -250) * mm, v(3000, -50) * mm], "startDerivative": vector(0, -722.87) * mm, "endDerivative": vector(7692.49, -256.42) * mm});
            skSolve(sketch);
        }
        {
            var Q0;
            Q0=qCreatedBy(makeId("Right.planeOp"),FACE);
            cPlane(context, id + "F46", {"entities" : qUnion([Q0]), "cplaneType" : CPlaneType.OFFSET, "offset" : 4600 * mm, "oppositeDirection" : true, "width" : 150 * mm, "height" : 150 * mm});
        }
        {
            var Q0;
            Q0=qCreatedBy(id+"F46.planeOp",FACE);
            var sketch = newSketch(context, id + "F47", { "sketchPlane" : qUnion([Q0])});
            skFitSpline(sketch, "E94", {"points": [v(-750, -10) * mm, v(250, 25) * mm, v(2250, -10) * mm], "startDerivative": vector(0, 162.94) * mm, "endDerivative": vector(5121.8, -51.22) * mm});
            skFitSpline(sketch, "E95", {"points": [v(-750, -10) * mm, v(750, -25) * mm, v(2250, -10) * mm], "startDerivative": vector(0, -60) * mm, "endDerivative": vector(6000, 0) * mm});
            skSolve(sketch);
        }
        {
            var Q0;
            Q0=qCreatedBy(makeId("Right.planeOp"),FACE);
            cPlane(context, id + "F48", {"entities" : qUnion([Q0]), "cplaneType" : CPlaneType.OFFSET, "offset" : 4600 * mm, "width" : 150 * mm, "height" : 150 * mm});
        }
        {
            var Q0;
            Q0=qCreatedBy(id+"F48.planeOp",FACE);
            var sketch = newSketch(context, id + "F49", { "sketchPlane" : qUnion([Q0])});
            skFitSpline(sketch, "E96", {"points": [v(-750, -10) * mm, v(250, 25) * mm, v(2250, -10) * mm], "startDerivative": vector(0, 253.46) * mm, "endDerivative": vector(3841.36, -51.22) * mm});
            skFitSpline(sketch, "E97", {"points": [v(-750, -10) * mm, v(750, -25) * mm, v(2250, -10) * mm], "startDerivative": vector(0, -45) * mm, "endDerivative": vector(4500, 0) * mm});
            skSolve(sketch);
        }
        {
            var Q0;
            Q0=qSketchRegion(id+"F41",true);
            extrude(context, id + "F50", {"entities" : qUnion([Q0]), "endBound" : BoundingType.SYMMETRIC, "depth" : 2500 * mm, "offsetDistance" : 25 * mm});
        }
        {
            var Q1;
            Q1=makeQuery(id+"F50.opExtrude","CAP_FACE",FACE,{"disambiguationData":[OSD([sQuery(id+"F41.wireOp",EDGE,"E89")])],"isStart":true});
            var Q2;
            {var subQ0=sQuery(id+"F43.wireOp",EDGE,"E90");Q2=makeQuery(id+"F43.imprint","IMPRINT",FACE,{"disambiguationData":[TD([[makeQuery(id+"F43.imprint","IMPRINT",EDGE,{"derivedFrom":subQ0}),-1.0]])]});}
            loft(context, id + "F51", {"operationType" : NewBodyOperationType.ADD, "sheetProfilesArray" : [{ "sheetProfileEntities" : qUnion([Q1]) }, { "sheetProfileEntities" : qUnion([Q2]) }]});
        }
        {
            var Q1;
            Q1=makeQuery(id+"F50.opExtrude","CAP_FACE",FACE,{"disambiguationData":[OSD([sQuery(id+"F41.wireOp",EDGE,"E89")])],"isStart":false});
            var Q2;
            {var subQ0=sQuery(id+"F45.wireOp",EDGE,"E92");Q2=makeQuery(id+"F45.imprint","IMPRINT",FACE,{"disambiguationData":[TD([[makeQuery(id+"F45.imprint","IMPRINT",EDGE,{"derivedFrom":subQ0}),-1.0]])]});}
            loft(context, id + "F52", {"operationType" : NewBodyOperationType.ADD, "sheetProfilesArray" : [{ "sheetProfileEntities" : qUnion([Q1]) }, { "sheetProfileEntities" : qUnion([Q2]) }]});
        }
        {
            var Q1;
            {var subQ0=sQuery(id+"F43.wireOp",EDGE,"E90");Q1=makeQuery(id+"F51.opLoft","CAP_FACE",FACE,{"disambiguationData":[OSD([makeQuery(id+"F43.imprint","IMPRINT",FACE,{"disambiguationData":[TD([[makeQuery(id+"F43.imprint","IMPRINT",EDGE,{"derivedFrom":subQ0}),-1.0]])]})])],"isStart":true});}
            var Q2;
            Q2=makeQuery(id+"F47.imprint","IMPRINT",FACE,{"disambiguationData":[TD([[makeQuery(id+"F47.imprint","IMPRINT",EDGE,{"derivedFrom":sQuery(id+"F47.wireOp",EDGE,"E94")}),-1.0]])]});
            loft(context, id + "F53", {"operationType" : NewBodyOperationType.ADD, "sheetProfilesArray" : [{ "sheetProfileEntities" : qUnion([Q1]) }, { "sheetProfileEntities" : qUnion([Q2]) }]});
        }
        {
            var Q1;
            {var subQ0=sQuery(id+"F45.wireOp",EDGE,"E92");Q1=makeQuery(id+"F52.opLoft","CAP_FACE",FACE,{"disambiguationData":[OSD([makeQuery(id+"F45.imprint","IMPRINT",FACE,{"disambiguationData":[TD([[makeQuery(id+"F45.imprint","IMPRINT",EDGE,{"derivedFrom":subQ0}),-1.0]])]})])],"isStart":true});}
            var Q2;
            Q2=makeQuery(id+"F49.imprint","IMPRINT",FACE,{"disambiguationData":[TD([[makeQuery(id+"F49.imprint","IMPRINT",EDGE,{"derivedFrom":sQuery(id+"F49.wireOp",EDGE,"E96")}),-1.0]])]});
            loft(context, id + "F54", {"operationType" : NewBodyOperationType.ADD, "sheetProfilesArray" : [{ "sheetProfileEntities" : qUnion([Q1]) }, { "sheetProfileEntities" : qUnion([Q2]) }]});
        }
        {
            var Q0;
            Q0=qCreatedBy(makeId("Right.planeOp"),FACE);
            var sketch = newSketch(context, id + "F55", { "sketchPlane" : qUnion([Q0])});
            skLineSegment(sketch, "E98", {"start": v(0, 0) * mm, "end": v(4500, 0) * mm});
            skLineSegment(sketch, "E99", {"start": v(4500, 0) * mm, "end": v(4500, 1000) * mm});
            skLineSegment(sketch, "E100", {"start": v(4500, 1000) * mm, "end": v(4500, 750) * mm});
            skLineSegment(sketch, "E101", {"start": v(4500, 750) * mm, "end": v(4000, 750) * mm});
            skLineSegment(sketch, "E102", {"start": v(4500, 750) * mm, "end": v(6250, 750) * mm});
            skLineSegment(sketch, "E103", {"start": v(4500, 1000) * mm, "end": v(4000, 1000) * mm});
            skLineSegment(sketch, "E104", {"start": v(4500, 1000) * mm, "end": v(6881.46, 1000) * mm});
            skLineSegment(sketch, "E105", {"start": v(6881.46, 1000) * mm, "end": v(8500, 1000) * mm});
            skLineSegment(sketch, "E106", {"start": v(8500, 1000) * mm, "end": v(8500, 2800) * mm});
            skLineSegment(sketch, "E107", {"start": v(6881.46, 1000) * mm, "end": v(7648.6, 2572.89) * mm});
            skLineSegment(sketch, "E108", {"start": v(7648.6, 2572.89) * mm, "end": v(5943.2, 2572.89) * mm});
            skLineSegment(sketch, "E109", {"start": v(4000, 1000) * mm, "end": v(5943.2, 2572.89) * mm});
            skSolve(sketch);
        }
        {
            var Q0;
            Q0=qCreatedBy(makeId("Top.planeOp"),FACE);
            cPlane(context, id + "F56", {"entities" : qUnion([Q0]), "cplaneType" : CPlaneType.OFFSET, "offset" : 750 * mm, "width" : 150 * mm, "height" : 150 * mm});
        }
        {
            var Q0;
            Q0=qCreatedBy(id+"F56.planeOp",FACE);
            var sketch = newSketch(context, id + "F57", { "sketchPlane" : qUnion([Q0])});
            skFitSpline(sketch, "E110", {"points": [v(0, 4000) * mm, v(-250, 4500) * mm, v(0, 6250) * mm], "startDerivative": vector(-889.86, 1147.1) * mm, "endDerivative": vector(737.87, 3164.53) * mm});
            skFitSpline(sketch, "E111", {"points": [v(0, 4000) * mm, v(250, 4500) * mm, v(0, 6250) * mm], "startDerivative": vector(889.86, 1147.1) * mm, "endDerivative": vector(-737.87, 3164.53) * mm});
            skSolve(sketch);
        }
        {
            var Q0;
            Q0=qCreatedBy(makeId("Top.planeOp"),FACE);
            cPlane(context, id + "F58", {"entities" : qUnion([Q0]), "cplaneType" : CPlaneType.OFFSET, "offset" : 1000 * mm, "width" : 150 * mm, "height" : 150 * mm});
        }
        {
            var Q0;
            Q0=qCreatedBy(id+"F58.planeOp",FACE);
            var sketch = newSketch(context, id + "F59", { "sketchPlane" : qUnion([Q0])});
            skFitSpline(sketch, "E112", {"points": [v(0, 4000) * mm, v(-250, 4500) * mm, v(0, 6881.46) * mm], "startDerivative": vector(0, 2302.24) * mm, "endDerivative": vector(0, 5298.17) * mm});
            skFitSpline(sketch, "E113", {"points": [v(0, 4000) * mm, v(250, 4500) * mm, v(0, 6881.46) * mm], "startDerivative": vector(0, 2302.24) * mm, "endDerivative": vector(0, 5298.17) * mm});
            skSolve(sketch);
        }
        {
            var Q0;
            Q0=sQuery(id+"F55.wireOp",EDGE,"E108");
            cPlane(context, id + "F60", {"entities" : qUnion([Q0]), "cplaneType" : CPlaneType.LINE_ANGLE, "offset" : 25 * mm, "angle" : 180 * degree, "width" : 150 * mm, "height" : 150 * mm});
        }
        {
            var Q0;
            Q0=qCreatedBy(id+"F60.planeOp",FACE);
            var sketch = newSketch(context, id + "F61", { "sketchPlane" : qUnion([Q0])});
            skFitSpline(sketch, "E114", {"points": [v(0, 5943.2) * mm, v(-25, 6795.9) * mm, v(0, 7648.6) * mm], "startDerivative": vector(-75, 1705.4) * mm, "endDerivative": vector(75, 1705.4) * mm});
            skFitSpline(sketch, "E115", {"points": [v(0, 5943.2) * mm, v(25, 6795.9) * mm, v(0, 7648.6) * mm], "startDerivative": vector(75, 1705.4) * mm, "endDerivative": vector(-75, 1705.4) * mm});
            skSolve(sketch);
        }
        {
            var Q0;
            Q0=qCreatedBy(makeId("Front.planeOp"),FACE);
            cPlane(context, id + "F62", {"entities" : qUnion([Q0]), "cplaneType" : CPlaneType.OFFSET, "offset" : 8500 * mm, "oppositeDirection" : true, "width" : 150 * mm, "height" : 150 * mm});
        }
        {
            var Q0;
            Q0=qCreatedBy(id+"F62.planeOp",FACE);
            var sketch = newSketch(context, id + "F63", { "sketchPlane" : qUnion([Q0])});
            skCircle(sketch, "E116", {"center": v(0, 2775) * mm, "radius": 25 * mm});
            skSolve(sketch);
        }
        {
            var Q0;
            Q0=qCreatedBy(makeId("Right.planeOp"),FACE);
            var sketch = newSketch(context, id + "F64", { "sketchPlane" : qUnion([Q0])});
            skLineSegment(sketch, "E117", {"start": v(5943.2, 2572.89) * mm, "end": v(8500, 2800) * mm});
            skSolve(sketch);
        }
        {
            var Q1;
            Q1=qSketchRegion(id+"F57",true);
            var Q2;
            Q2=qSketchRegion(id+"F59",true);
            loft(context, id + "F65", {"sheetProfilesArray" : [{ "sheetProfileEntities" : qUnion([Q1]) }, { "sheetProfileEntities" : qUnion([Q2]) }]});
        }
        {
            var Q1;
            {var subQ0=sQuery(id+"F59.wireOp",EDGE,"E112");Q1=makeQuery(id+"F65.opLoft","CAP_FACE",FACE,{"disambiguationData":[OSD([makeQuery(id+"F59.imprint","IMPRINT",FACE,{"disambiguationData":[TD([[makeQuery(id+"F59.imprint","IMPRINT",EDGE,{"derivedFrom":subQ0}),-1.0]])]})])],"isStart":true});}
            var Q2;
            Q2=makeQuery(id+"F61.imprint","IMPRINT",FACE,{"disambiguationData":[TD([[makeQuery(id+"F61.imprint","IMPRINT",EDGE,{"derivedFrom":sQuery(id+"F61.wireOp",EDGE,"E114")}),-1.0]])]});
            loft(context, id + "F66", {"operationType" : NewBodyOperationType.ADD, "sheetProfilesArray" : [{ "sheetProfileEntities" : qUnion([Q1]) }, { "sheetProfileEntities" : qUnion([Q2]) }]});
        }
        {
            var Q1;
            Q1=makeQuery(id+"F66.opLoft","CAP_FACE",FACE,{"disambiguationData":[OSD([makeQuery(id+"F61.imprint","IMPRINT",FACE,{"disambiguationData":[TD([[makeQuery(id+"F61.imprint","IMPRINT",EDGE,{"derivedFrom":sQuery(id+"F61.wireOp",EDGE,"E114")}),-1.0]])]})])],"isStart":true});
            var Q2;
            Q2=makeQuery(id+"F63.imprint","IMPRINT",FACE,{"disambiguationData":[TD([[makeQuery(id+"F63.imprint","IMPRINT",EDGE,{"derivedFrom":sQuery(id+"F63.wireOp",EDGE,"E116")}),1.0]])]});
            var Q3;
            Q3=sQuery(id+"F64.wireOp",EDGE,"E117");
            loft(context, id + "F67", {"operationType" : NewBodyOperationType.ADD, "addGuides" : true, "sheetProfilesArray" : [{ "sheetProfileEntities" : qUnion([Q1]) }, { "sheetProfileEntities" : qUnion([Q2]) }], "guidesArray" : [{ "guideEntities" : qUnion([Q3]), "guideDerivativeType" : LoftGuideDerivativeType.DEFAULT, "guideDerivativeMagnitude" : 1 }]});
        }
        {
            var Q0;
            Q0=qCreatedBy(makeId("Top.planeOp"),FACE);
            cPlane(context, id + "F68", {"entities" : qUnion([Q0]), "cplaneType" : CPlaneType.OFFSET, "offset" : 2000 * mm, "width" : 150 * mm, "height" : 150 * mm});
        }
        {
            var Q0;
            Q0=qCreatedBy(id+"F68.planeOp",FACE);
            var sketch = newSketch(context, id + "F69", { "sketchPlane" : qUnion([Q0])});
            skLineSegment(sketch, "E118", {"start": v(0, 0) * mm, "end": v(0, 4500) * mm});
            skLineSegment(sketch, "E119", {"start": v(0, 4500) * mm, "end": v(0, 7369.2) * mm});
            skLineSegment(sketch, "E120", {"start": v(0, 7369.2) * mm, "end": v(0, 5235.43) * mm});
            skLineSegment(sketch, "E121", {"start": v(0, 6302.31) * mm, "end": v(0, 5302.31) * mm});
            skLineSegment(sketch, "E122", {"start": v(0, 6302.31) * mm, "end": v(0, 7302.31) * mm});
            skLineSegment(sketch, "E123", {"start": v(0, 6302.31) * mm, "end": v(0, 6552.31) * mm});
            skLineSegment(sketch, "E124", {"start": v(0, 6302.31) * mm, "end": v(-1200, 6302.31) * mm});
            skLineSegment(sketch, "E125", {"start": v(0, 6302.31) * mm, "end": v(1200, 6302.31) * mm});
            skLineSegment(sketch, "E126", {"start": v(0, 6552.31) * mm, "end": v(-1700, 6552.31) * mm});
            skLineSegment(sketch, "E127", {"start": v(0, 6552.31) * mm, "end": v(1700, 6552.31) * mm});
            skLineSegment(sketch, "E128", {"start": v(0, 7302.31) * mm, "end": v(-2000, 7302.31) * mm});
            skLineSegment(sketch, "E129", {"start": v(0, 7302.31) * mm, "end": v(2000, 7302.31) * mm});
            skLineSegment(sketch, "E130", {"start": v(-2000, 7302.31) * mm, "end": v(-2000, 7052.31) * mm});
            skLineSegment(sketch, "E131", {"start": v(2000, 7302.31) * mm, "end": v(2000, 7052.31) * mm});
            skFitSpline(sketch, "E132", {"points": [v(0, 5302.31) * mm, v(-1200, 6302.31) * mm, v(-2000, 7052.31) * mm], "startDerivative": vector(0, 5513.6) * mm, "endDerivative": vector(-1974.16, 3290.27) * mm});
            skFitSpline(sketch, "E133", {"points": [v(0, 5302.31) * mm, v(1200, 6302.31) * mm, v(2000, 7052.31) * mm], "startDerivative": vector(0, 5513.6) * mm, "endDerivative": vector(1974.16, 3290.27) * mm});
            skFitSpline(sketch, "E134", {"points": [v(0, 6552.31) * mm, v(-2000, 7302.31) * mm], "startDerivative": vector(0, 2250) * mm, "endDerivative": vector(-900, 2250) * mm});
            skFitSpline(sketch, "E135", {"points": [v(0, 6552.31) * mm, v(2000, 7302.31) * mm], "startDerivative": vector(0, 2250) * mm, "endDerivative": vector(900, 2250) * mm});
            skSolve(sketch);
        }
        {
            var Q0;
            Q0=qCreatedBy(makeId("Right.planeOp"),FACE);
            var sketch = newSketch(context, id + "F70", { "sketchPlane" : qUnion([Q0])});
            skFitSpline(sketch, "E136", {"points": [v(5302.31, 2000) * mm, v(5927.31, 2050) * mm, v(6552.31, 2000) * mm], "startDerivative": vector(1250, 150) * mm, "endDerivative": vector(1250, -150) * mm});
            skFitSpline(sketch, "E137", {"points": [v(5302.31, 2000) * mm, v(5927.31, 1950) * mm, v(6552.31, 2000) * mm], "startDerivative": vector(1250, -150) * mm, "endDerivative": vector(1250, 150) * mm});
            skSolve(sketch);
        }
        {
            var Q0;
            Q0=qCreatedBy(makeId("Right.planeOp"),FACE);
            cPlane(context, id + "F71", {"entities" : qUnion([Q0]), "cplaneType" : CPlaneType.OFFSET, "offset" : 2000 * mm, "oppositeDirection" : true, "width" : 150 * mm, "height" : 150 * mm});
        }
        {
            var Q0;
            Q0=qCreatedBy(id+"F71.planeOp",FACE);
            var sketch = newSketch(context, id + "F72", { "sketchPlane" : qUnion([Q0])});
            skFitSpline(sketch, "E138", {"points": [v(7052.31, 2000) * mm, v(7177.31, 2010) * mm, v(7302.31, 2000) * mm], "startDerivative": vector(250, 30) * mm, "endDerivative": vector(250, -30) * mm});
            skFitSpline(sketch, "E139", {"points": [v(7052.31, 2000) * mm, v(7177.31, 1990) * mm, v(7302.31, 2000) * mm], "startDerivative": vector(250, -30) * mm, "endDerivative": vector(250, 30) * mm});
            skSolve(sketch);
        }
        {
            var Q0;
            Q0=qCreatedBy(makeId("Right.planeOp"),FACE);
            cPlane(context, id + "F73", {"entities" : qUnion([Q0]), "cplaneType" : CPlaneType.OFFSET, "offset" : 2000 * mm, "width" : 150 * mm, "height" : 150 * mm});
        }
        {
            var Q0;
            Q0=qCreatedBy(id+"F73.planeOp",FACE);
            var sketch = newSketch(context, id + "F74", { "sketchPlane" : qUnion([Q0])});
            skFitSpline(sketch, "E140", {"points": [v(7052.31, 2000) * mm, v(7177.31, 2010) * mm, v(7302.31, 2000) * mm], "startDerivative": vector(250, 30) * mm, "endDerivative": vector(250, -30) * mm});
            skFitSpline(sketch, "E141", {"points": [v(7052.31, 2000) * mm, v(7177.31, 1990) * mm, v(7302.31, 2000) * mm], "startDerivative": vector(250, -30) * mm, "endDerivative": vector(250, 30) * mm});
            skSolve(sketch);
        }
        {
            var Q1;
            Q1=qSketchRegion(id+"F70",true);
            var Q2;
            Q2=makeQuery(id+"F72.imprint","IMPRINT",FACE,{"disambiguationData":[TD([[makeQuery(id+"F72.imprint","IMPRINT",EDGE,{"derivedFrom":sQuery(id+"F72.wireOp",EDGE,"E138")}),-1.0]])]});
            var Q3;
            Q3=sQuery(id+"F69.wireOp",EDGE,"E132");
            var Q4;
            Q4=sQuery(id+"F69.wireOp",EDGE,"E134");
            loft(context, id + "F75", {"addGuides" : true, "sheetProfilesArray" : [{ "sheetProfileEntities" : qUnion([Q1]) }, { "sheetProfileEntities" : qUnion([Q2]) }], "guidesArray" : [{ "guideEntities" : qUnion([Q3]), "guideDerivativeType" : LoftGuideDerivativeType.DEFAULT, "guideDerivativeMagnitude" : 1 }, { "guideEntities" : qUnion([Q4]), "guideDerivativeType" : LoftGuideDerivativeType.DEFAULT, "guideDerivativeMagnitude" : 1 }]});
        }
        {
            var Q1;
            Q1=qSketchRegion(id+"F70",true);
            var Q2;
            Q2=makeQuery(id+"F74.imprint","IMPRINT",FACE,{"disambiguationData":[TD([[makeQuery(id+"F74.imprint","IMPRINT",EDGE,{"derivedFrom":sQuery(id+"F74.wireOp",EDGE,"E140")}),-1.0]])]});
            var Q3;
            Q3=sQuery(id+"F69.wireOp",EDGE,"E133");
            var Q4;
            Q4=sQuery(id+"F69.wireOp",EDGE,"E135");
            loft(context, id + "F76", {"operationType" : NewBodyOperationType.ADD, "addGuides" : true, "sheetProfilesArray" : [{ "sheetProfileEntities" : qUnion([Q1]) }, { "sheetProfileEntities" : qUnion([Q2]) }], "guidesArray" : [{ "guideEntities" : qUnion([Q3]), "guideDerivativeType" : LoftGuideDerivativeType.DEFAULT, "guideDerivativeMagnitude" : 1 }, { "guideEntities" : qUnion([Q4]), "guideDerivativeType" : LoftGuideDerivativeType.DEFAULT, "guideDerivativeMagnitude" : 1 }]});
        }
    });
